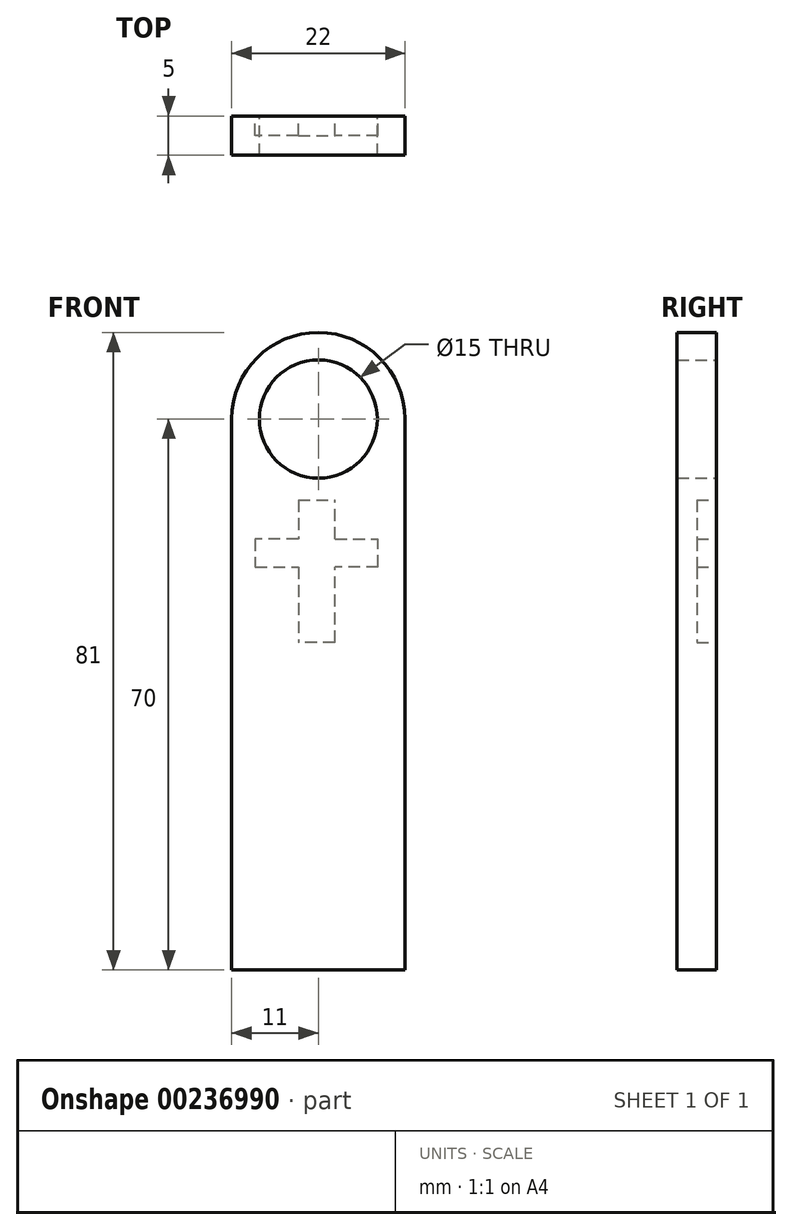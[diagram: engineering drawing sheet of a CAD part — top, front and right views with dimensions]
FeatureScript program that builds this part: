
annotation { "Feature Type Name" : "Feature", "Feature Type Description" : "" }
export const myFeature = defineFeature(function(context is Context, id is Id, definition is map)
    precondition{}
    {
        {
            var Q0;
            Q0=qCreatedBy(makeId("Front.planeOp"),FACE);
            var sketch = newSketch(context, id + "F0", { "sketchPlane" : qUnion([Q0])});
            skLineSegment(sketch, "E0.top", {"start": v(-22, 0) * mm, "end": v(0, 0) * mm});
            skLineSegment(sketch, "E0.left", {"start": v(-22, 70) * mm, "end": v(-22, 0) * mm});
            skLineSegment(sketch, "E0.right", {"start": v(0, 70) * mm, "end": v(0, 0) * mm});
            skArc(sketch, "E1", {"start": v(0, 70) * mm, "mid": v(-11, 81) * mm, "end": v(-22, 70) * mm});
            skCircle(sketch, "E2", {"center": v(-11, 70) * mm, "radius": 7.5 * mm});
            skSolve(sketch);
        }
        {
            var Q0;
            Q0=makeQuery(id+"F0.imprint","IMPRINT",FACE,{"disambiguationData":[TD([[makeQuery(id+"F0.imprint","IMPRINT",EDGE,{"derivedFrom":sQuery(id+"F0.wireOp",EDGE,"E0.top")}),1.0]])]});
            extrude(context, id + "F1", {"entities" : qUnion([Q0]), "depth" : 5 * mm});
        }
        {
            var Q0;
            Q0=qCreatedBy(makeId("Front.planeOp"),FACE);
            var sketch = newSketch(context, id + "F2", { "sketchPlane" : qUnion([Q0])});
            skLineSegment(sketch, "E3", {"start": v(-13.54, 59.7) * mm, "end": v(-13.54, 54.77) * mm});
            skLineSegment(sketch, "E4", {"start": v(-13.54, 54.77) * mm, "end": v(-19.02, 54.77) * mm});
            skLineSegment(sketch, "E5", {"start": v(-19.02, 54.77) * mm, "end": v(-19.02, 51.2) * mm});
            skLineSegment(sketch, "E6", {"start": v(-19.02, 51.2) * mm, "end": v(-13.54, 51.2) * mm});
            skLineSegment(sketch, "E7", {"start": v(-13.54, 51.2) * mm, "end": v(-13.54, 41.61) * mm});
            skLineSegment(sketch, "E8", {"start": v(-13.54, 41.61) * mm, "end": v(-13.54, 51.2) * mm});
            skLineSegment(sketch, "E9", {"start": v(-13.54, 59.7) * mm, "end": v(-8.88, 59.7) * mm});
            skLineSegment(sketch, "E10", {"start": v(-8.88, 54.77) * mm, "end": v(-8.88, 59.7) * mm});
            skLineSegment(sketch, "E11", {"start": v(-8.88, 54.77) * mm, "end": v(-3.4, 54.77) * mm});
            skLineSegment(sketch, "E12", {"start": v(-3.4, 51.2) * mm, "end": v(-3.4, 54.77) * mm});
            skLineSegment(sketch, "E13", {"start": v(-3.4, 51.2) * mm, "end": v(-8.88, 51.2) * mm});
            skLineSegment(sketch, "E14", {"start": v(-8.88, 41.61) * mm, "end": v(-8.88, 51.2) * mm});
            skLineSegment(sketch, "E15", {"start": v(-8.88, 41.61) * mm, "end": v(-13.54, 41.61) * mm});
            skLineSegment(sketch, "E16.trimOffspring", {"start": v(-13.54, 54.77) * mm, "end": v(-13.54, 59.7) * mm});
            skSolve(sketch);
        }
        {
            var Q0;
            Q0=makeQuery(id+"F2.imprint","IMPRINT",FACE,{"disambiguationData":[TD([[makeQuery(id+"F2.imprint","IMPRINT",EDGE,{"derivedFrom":sQuery(id+"F2.wireOp",EDGE,"E4")}),1.0]])]});
            extrude(context, id + "F3", {"entities" : qUnion([Q0]), "operationType" : NewBodyOperationType.REMOVE, "depth" : 2.5 * mm});
        }
    });
